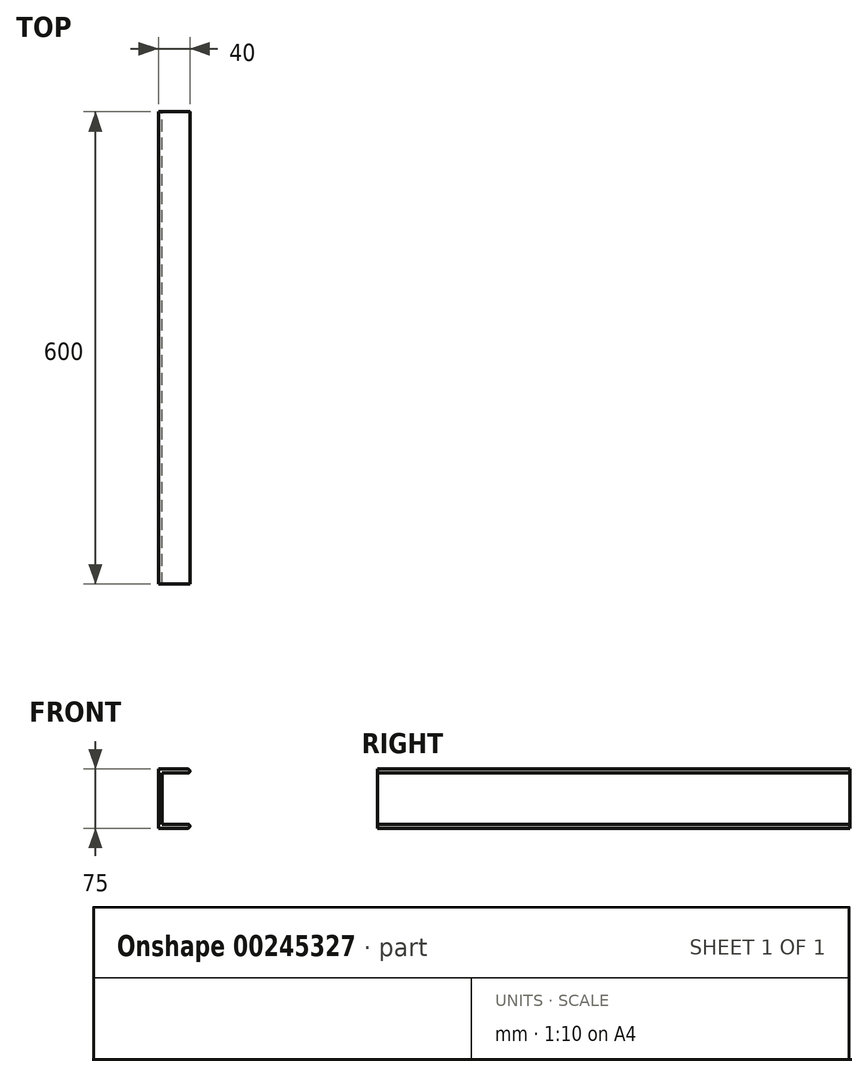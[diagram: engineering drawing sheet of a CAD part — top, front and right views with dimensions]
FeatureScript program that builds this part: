
annotation { "Feature Type Name" : "Feature", "Feature Type Description" : "" }
export const myFeature = defineFeature(function(context is Context, id is Id, definition is map)
    precondition{}
    {
        {
            var Q0;
            Q0=qCreatedBy(makeId("Front.planeOp"),FACE);
            var sketch = newSketch(context, id + "F0", { "sketchPlane" : qUnion([Q0])});
            skLineSegment(sketch, "E0", {"start": v(0, 0) * mm, "end": v(37.5, 0) * mm});
            skLineSegment(sketch, "E1", {"start": v(40, 2.5) * mm, "end": v(40, 2.5) * mm});
            skLineSegment(sketch, "E2", {"start": v(37.5, 5) * mm, "end": v(5, 5) * mm});
            skLineSegment(sketch, "E3", {"start": v(5, 5) * mm, "end": v(5, 70) * mm});
            skLineSegment(sketch, "E4", {"start": v(5, 70) * mm, "end": v(37.5, 70) * mm});
            skLineSegment(sketch, "E5", {"start": v(40, 72.5) * mm, "end": v(40, 72.5) * mm});
            skLineSegment(sketch, "E6", {"start": v(37.5, 75) * mm, "end": v(0, 75) * mm});
            skLineSegment(sketch, "E7", {"start": v(0, 75) * mm, "end": v(0, 0) * mm});
            skPoint(sketch, "E8.visualSharp", {"position": v(40, 75) * mm});
            skArc(sketch, "E8.filletArc", {"start": v(40, 72.5) * mm, "mid": v(39.27, 74.27) * mm, "end": v(37.5, 75) * mm});
            skPoint(sketch, "E9.visualSharp", {"position": v(40, 70) * mm});
            skArc(sketch, "E9.filletArc", {"start": v(37.5, 70) * mm, "mid": v(39.27, 70.73) * mm, "end": v(40, 72.5) * mm});
            skPoint(sketch, "E10.visualSharp", {"position": v(40, 5) * mm});
            skArc(sketch, "E10.filletArc", {"start": v(40, 2.5) * mm, "mid": v(39.27, 4.27) * mm, "end": v(37.5, 5) * mm});
            skPoint(sketch, "E11.visualSharp", {"position": v(40, 0) * mm});
            skArc(sketch, "E11.filletArc", {"start": v(37.5, 0) * mm, "mid": v(39.27, 0.73) * mm, "end": v(40, 2.5) * mm});
            skSolve(sketch);
        }
        {
            var Q0;
            Q0 = qSketchRegion(id + "F0", true);
            extrude(context, id + "F1", {"entities" : qUnion([Q0]), "depth" : 600 * mm});
        }
    });
